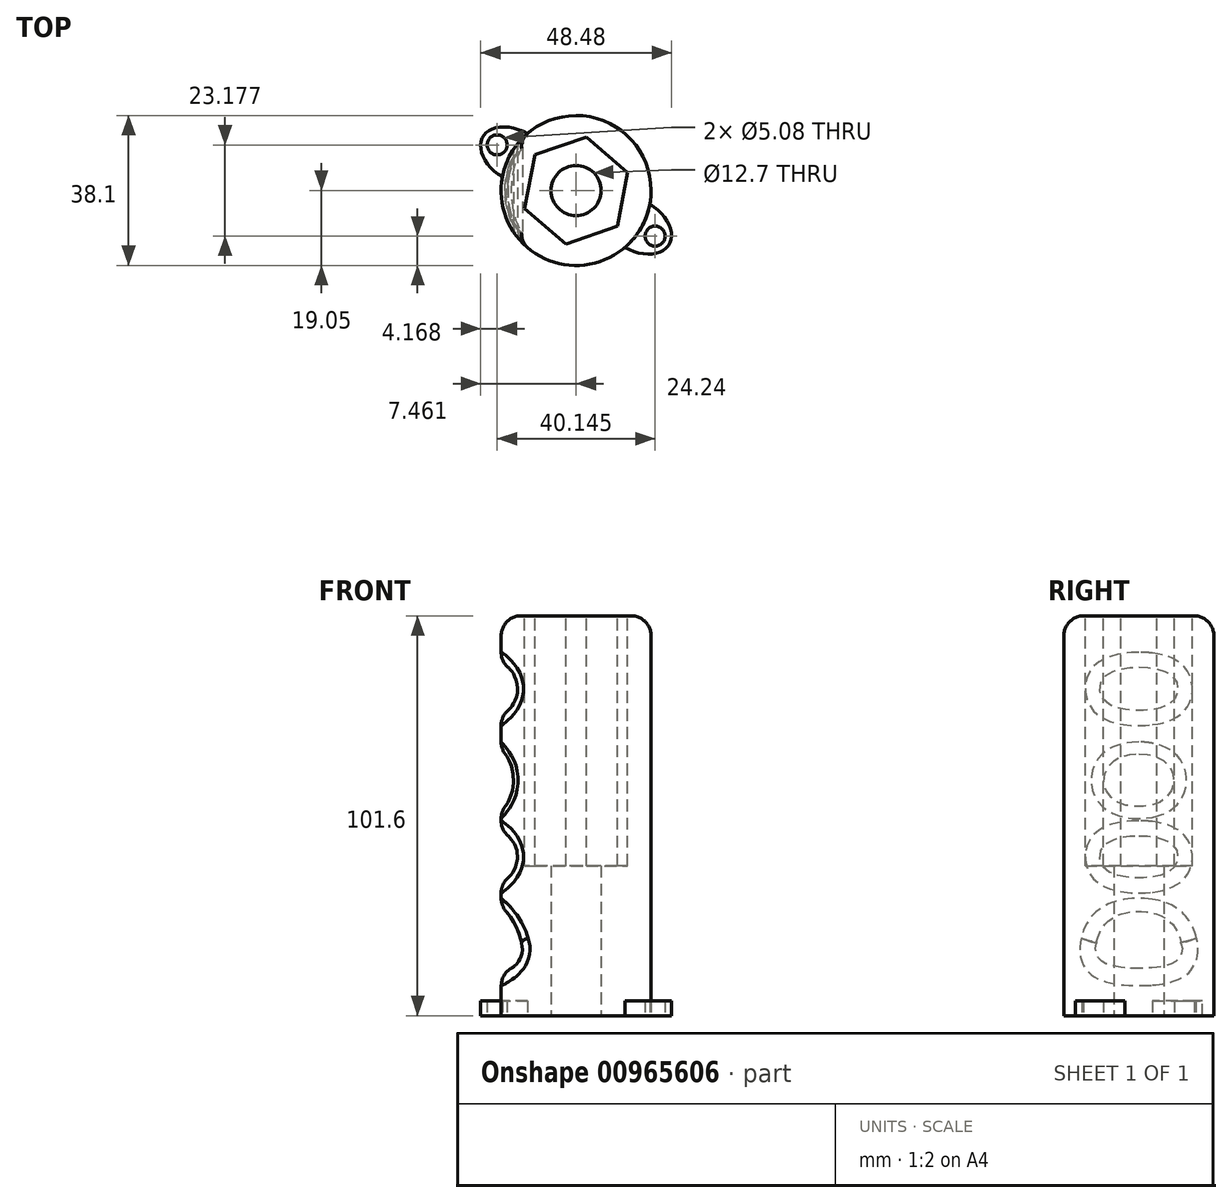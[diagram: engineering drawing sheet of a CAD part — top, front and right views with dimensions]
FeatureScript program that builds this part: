
annotation { "Feature Type Name" : "Feature", "Feature Type Description" : "" }
export const myFeature = defineFeature(function(context is Context, id is Id, definition is map)
    precondition{}
    {
        {
            var Q0;
            Q0=qCreatedBy(makeId("Top.planeOp"),FACE);
            var sketch = newSketch(context, id + "F0", { "sketchPlane" : qUnion([Q0])});
            skCircle(sketch, "E0", {"center": v(0, 0) * mm, "radius": 19.05 * mm});
            skSolve(sketch);
        }
        {
            var Q0;
            Q0=makeQuery(id+"F0.imprint","IMPRINT",FACE,{"disambiguationData":[TD([[makeQuery(id+"F0.imprint","IMPRINT",EDGE,{"derivedFrom":sQuery(id+"F0.wireOp",EDGE,"E0")}),1.0]])]});
            extrude(context, id + "F1", {"entities" : qUnion([Q0]), "depth" : 101.6 * mm, "offsetDistance" : 25.4 * mm});
        }
        {
            var Q0;
            Q0=qCreatedBy(makeId("Front.planeOp"),FACE);
            cPlane(context, id + "F2", {"entities" : qUnion([Q0]), "cplaneType" : CPlaneType.OFFSET, "offset" : 19.05 * mm, "width" : 152.4 * mm, "height" : 152.4 * mm});
        }
        {
            var Q0;
            Q0=qCreatedBy(id+"F2.planeOp",FACE);
            var sketch = newSketch(context, id + "F3", { "sketchPlane" : qUnion([Q0])});
            skLineSegment(sketch, "E1", {"start": v(0, 0) * mm, "end": v(-12.7, 0) * mm});
            skLineSegment(sketch, "E2", {"start": v(0, 0) * mm, "end": v(-16.51, 0) * mm});
            skLineSegment(sketch, "E3", {"start": v(-19.05, 0) * mm, "end": v(-19.05, 101.6) * mm});
            skLineSegment(sketch, "E4.0", {"start": v(-19.05, 101.6) * mm, "end": v(19.05, 101.6) * mm});
            skLineSegment(sketch, "E5", {"start": v(-16.51, 0) * mm, "end": v(-16.51, 101.6) * mm, "construction": true});
            skLineSegment(sketch, "E6", {"start": v(-12.7, 0) * mm, "end": v(-12.7, 101.6) * mm});
            skLineSegment(sketch, "E7", {"start": v(0, 0) * mm, "end": v(19.05, 0) * mm});
            skLineSegment(sketch, "E8", {"start": v(19.05, 0) * mm, "end": v(19.05, 11.29) * mm});
            skLineSegment(sketch, "E9", {"start": v(19.05, 11.29) * mm, "end": v(19.05, 22.58) * mm});
            skLineSegment(sketch, "E10", {"start": v(19.05, 22.58) * mm, "end": v(19.05, 33.87) * mm});
            skLineSegment(sketch, "E11", {"start": v(19.05, 45.16) * mm, "end": v(19.05, 56.44) * mm});
            skLineSegment(sketch, "E12", {"start": v(19.05, 56.44) * mm, "end": v(19.05, 67.73) * mm});
            skLineSegment(sketch, "E13", {"start": v(19.05, 67.73) * mm, "end": v(19.05, 79.02) * mm});
            skLineSegment(sketch, "E14", {"start": v(19.05, 79.02) * mm, "end": v(19.05, 90.31) * mm});
            skLineSegment(sketch, "E15", {"start": v(19.05, 33.87) * mm, "end": v(19.05, 45.16) * mm});
            skLineSegment(sketch, "E16", {"start": v(19.05, 90.31) * mm, "end": v(19.05, 101.6) * mm});
            skArc(sketch, "E17", {"start": v(-19.05, 11.29) * mm, "mid": v(-14.7, 13.66) * mm, "end": v(-13.9, 18.54) * mm});
            skArc(sketch, "E18", {"start": v(-19.05, 33.87) * mm, "mid": v(-14.87, 40.34) * mm, "end": v(-19.05, 46.82) * mm});
            skArc(sketch, "E19", {"start": v(-19.05, 51.93) * mm, "mid": v(-15.88, 59.82) * mm, "end": v(-19.05, 67.71) * mm});
            skArc(sketch, "E20", {"start": v(-19.05, 76.38) * mm, "mid": v(-14.87, 83.03) * mm, "end": v(-19.05, 89.68) * mm});
            skArc(sketch, "E21", {"start": v(-13.9, 18.54) * mm, "mid": v(-15.74, 23.57) * mm, "end": v(-19.05, 27.79) * mm});
            skPoint(sketch, "E22.orphan", {"position": v(-19.05, 22.58) * mm});
            skSolve(sketch);
        }
        {
            var Q0;
            {var subQ0=sQuery(id+"F3.wireOp",EDGE,"E17");Q0=makeQuery(id+"F3.imprint","IMPRINT",FACE,{"disambiguationData":[TD([[makeQuery(id+"F3.imprint","IMPRINT",EDGE,{"derivedFrom":subQ0}),1.0]])]});}
            var Q1;
            {var subQ0=sQuery(id+"F3.wireOp",EDGE,"E18");Q1=makeQuery(id+"F3.imprint","IMPRINT",FACE,{"disambiguationData":[TD([[makeQuery(id+"F3.imprint","IMPRINT",EDGE,{"derivedFrom":subQ0}),1.0]])]});}
            var Q2;
            {var subQ0=sQuery(id+"F3.wireOp",EDGE,"E19");Q2=makeQuery(id+"F3.imprint","IMPRINT",FACE,{"disambiguationData":[TD([[makeQuery(id+"F3.imprint","IMPRINT",EDGE,{"derivedFrom":subQ0}),1.0]])]});}
            var Q3;
            {var subQ0=sQuery(id+"F3.wireOp",EDGE,"E20");Q3=makeQuery(id+"F3.imprint","IMPRINT",FACE,{"disambiguationData":[TD([[makeQuery(id+"F3.imprint","IMPRINT",EDGE,{"derivedFrom":subQ0}),1.0]])]});}
            extrude(context, id + "F4", {"entities" : qUnion([Q0, Q1, Q2, Q3]), "operationType" : NewBodyOperationType.REMOVE, "oppositeDirection" : true, "depth" : 50.8 * mm, "offsetDistance" : 25.4 * mm});
        }
        {
            var Q0;
            Q0=makeQuery(id+"F4.boolean.opBoolean","INTERSECT",EDGE,{"derivedFrom":[makeQuery(id+"F1.opExtrude","SWEPT_FACE",FACE,{"disambiguationData":[OSD([sQuery(id+"F0.wireOp",EDGE,"E0")])]}),makeQuery(id+"F4.opExtrude","SWEPT_FACE",FACE,{"disambiguationData":[OSD([sQuery(id+"F3.wireOp",EDGE,"E18")])]})]});
            var Q1;
            Q1=makeQuery(id+"F4.boolean.opBoolean","INTERSECT",EDGE,{"derivedFrom":[makeQuery(id+"F1.opExtrude","SWEPT_FACE",FACE,{"disambiguationData":[OSD([sQuery(id+"F0.wireOp",EDGE,"E0")])]}),makeQuery(id+"F4.opExtrude","SWEPT_FACE",FACE,{"disambiguationData":[OSD([sQuery(id+"F3.wireOp",EDGE,"E19")])]})]});
            var Q2;
            Q2=makeQuery(id+"F4.boolean.opBoolean","INTERSECT",EDGE,{"derivedFrom":[makeQuery(id+"F1.opExtrude","SWEPT_FACE",FACE,{"disambiguationData":[OSD([sQuery(id+"F0.wireOp",EDGE,"E0")])]}),makeQuery(id+"F4.opExtrude","SWEPT_FACE",FACE,{"disambiguationData":[OSD([sQuery(id+"F3.wireOp",EDGE,"E20")])]})]});
            var Q3;
            Q3=makeQuery(id+"F4.boolean.opBoolean","COPY",EDGE,{"derivedFrom":makeQuery(id+"F4.opExtrude","SWEPT_EDGE",EDGE,{"disambiguationData":[OSD([sQuery(id+"F3.wireOp",EDGE,"E17"),sQuery(id+"F3.wireOp",EDGE,"E21")])]})});
            var Q4;
            Q4=makeQuery(id+"F4.boolean.opBoolean","INTERSECT",EDGE,{"derivedFrom":[makeQuery(id+"F1.opExtrude","SWEPT_FACE",FACE,{"disambiguationData":[OSD([sQuery(id+"F0.wireOp",EDGE,"E0")])]}),makeQuery(id+"F4.opExtrude","SWEPT_FACE",FACE,{"disambiguationData":[OSD([sQuery(id+"F3.wireOp",EDGE,"E17")])]})]});
            var Q5;
            Q5=makeQuery(id+"F4.boolean.opBoolean","INTERSECT",EDGE,{"derivedFrom":[makeQuery(id+"F1.opExtrude","SWEPT_FACE",FACE,{"disambiguationData":[OSD([sQuery(id+"F0.wireOp",EDGE,"E0")])]}),makeQuery(id+"F4.opExtrude","SWEPT_FACE",FACE,{"disambiguationData":[OSD([sQuery(id+"F3.wireOp",EDGE,"E21")])]})]});
            fillet(context, id + "F5", {"entities" : qUnion([Q0, Q1, Q2, Q3, Q4, Q5]), "radius" : 5.08 * mm, "tangentPropagation" : true, "defaultsChanged" : false, "vertexSettings" : [], "allowEdgeOverflow" : false});
        }
        {
            var Q0;
            Q0=makeQuery(id+"F1.opExtrude","CAP_FACE",FACE,{"disambiguationData":[OSD([sQuery(id+"F0.wireOp",EDGE,"E0")])],"isStart":true});
            var sketch = newSketch(context, id + "F6", { "sketchPlane" : qUnion([Q0])});
            skLineSegment(sketch, "E23", {"start": v(0, 0) * mm, "end": v(0, 17.78) * mm});
            skLineSegment(sketch, "E24", {"start": v(0, 0) * mm, "end": v(-5.87, 0) * mm});
            skCircle(sketch, "E25.0.0", {"center": v(0, 0) * mm, "radius": 19.05 * mm});
            skLineSegment(sketch, "E26", {"start": v(0, 0) * mm, "end": v(17.78, 0) * mm});
            skEllipse(sketch, "E27.MirrorC", {"center": v(-15.4, -8.9) * mm, "majorRadius": 9.53 * mm, "minorRadius": 6.35 * mm, "majorAxis": v(-0.87, -0.5)});
            skLineSegment(sketch, "E28", {"start": v(0, 0) * mm, "end": v(21.59, 0) * mm, "construction": true});
            skLineSegment(sketch, "E29", {"start": v(-15.4, -8.9) * mm, "end": v(0, 0) * mm});
            skLineSegment(sketch, "E30", {"start": v(0, 0) * mm, "end": v(5.2, -9) * mm});
            skEllipse(sketch, "E31.MirrorC", {"center": v(15.4, 8.9) * mm, "majorRadius": 9.53 * mm, "minorRadius": 6.35 * mm, "majorAxis": v(0.87, 0.5)});
            skLineSegment(sketch, "E32", {"start": v(-15.4, -8.9) * mm, "end": v(-7.15, -4.13) * mm});
            skLineSegment(sketch, "E33", {"start": v(-23.65, -13.65) * mm, "end": v(-16.5, -9.53) * mm});
            skPoint(sketch, "E34", {"position": v(-20.07, -11.59) * mm});
            skPoint(sketch, "E35.MirrorP", {"position": v(20.07, 11.59) * mm});
            skSolve(sketch);
        }
        {
            var Q0;
            {var subQ0=sQuery(id+"FZY5milzs4ELDXf_1.wireOp",EDGE,"5038e947-432d-46be-ba0d-5f1da9be2be5.0.0");Q0=makeQuery(id+"FJVRa8w2PpgUHNq_1.boolean.opBoolean","MERGE",FACE,{"derivedFrom":[makeQuery(id+"F1.opExtrude","CAP_FACE",FACE,{"disambiguationData":[OSD([sQuery(id+"F0.wireOp",EDGE,"E0")])],"isStart":false}),makeQuery(id+"FJVRa8w2PpgUHNq_1.opExtrude","CAP_FACE",FACE,{"disambiguationData":[OSD([sQuery(id+"FZY5milzs4ELDXf_1.wireOp",EDGE,"e975b173-eecc-4d75-a19c-4a433cebcd96.0.0"),subQ0])],"isStart":true}),makeQuery(id+"FJVRa8w2PpgUHNq_1.opExtrude","CAP_FACE",FACE,{"disambiguationData":[OSD([sQuery(id+"FZY5milzs4ELDXf_1.wireOp",EDGE,"1aa8e91c-0e7e-4a1b-bd8e-dbe82b9d2f2e.0.0"),subQ0])],"isStart":true})]});}
            fillet(context, id + "F7", {"entities" : qUnion([Q0]), "radius" : 5.08 * mm, "tangentPropagation" : true, "allowEdgeOverflow" : false});
        }
        {
            var Q0;
            {var subQ0=sQuery(id+"F6.wireOp",EDGE,"E25.0.0");var subQ1=sQuery(id+"F6.wireOp",EDGE,"E27.MirrorC");var subQ2=makeQuery(id+"F6.imprint","INTERSECT",VERTEX,{"disambiguationData":[OD(0.0)],"derivedFrom":[subQ1,subQ0]});Q0=makeQuery(id+"F6.imprint","IMPRINT",FACE,{"disambiguationData":[TD([[makeQuery(id+"F6.imprint","IMPRINT",EDGE,{"disambiguationData":[TD([[subQ2,1.0]])],"derivedFrom":subQ1}),1.0]])]});}
            var Q1;
            {var subQ0=sQuery(id+"F6.wireOp",EDGE,"E25.0.0");var subQ1=sQuery(id+"F6.wireOp",EDGE,"foFyNaQt-y216-XrTq-2MQ0-xOWPkpz0StqU");var subQ2=makeQuery(id+"F6.imprint","INTERSECT",VERTEX,{"disambiguationData":[OD(0.0)],"derivedFrom":[subQ1,subQ0]});Q1=makeQuery(id+"F6.imprint","IMPRINT",FACE,{"disambiguationData":[TD([[makeQuery(id+"F6.imprint","IMPRINT",EDGE,{"disambiguationData":[TD([[subQ2,1.0]])],"derivedFrom":subQ1}),1.0]])]});}
            var Q2;
            {var subQ0=sQuery(id+"F6.wireOp",EDGE,"E31.MirrorC");var subQ1=sQuery(id+"F6.wireOp",EDGE,"E25.0.0");var subQ2=makeQuery(id+"F6.imprint","INTERSECT",VERTEX,{"disambiguationData":[OD(0.0)],"derivedFrom":[subQ1,subQ0]});Q2=makeQuery(id+"F6.imprint","IMPRINT",FACE,{"disambiguationData":[TD([[makeQuery(id+"F6.imprint","IMPRINT",EDGE,{"disambiguationData":[TD([[subQ2,-1.0]])],"derivedFrom":subQ1}),1.0]])]});}
            var Q3;
            {var subQ0=sQuery(id+"F6.wireOp",EDGE,"E33");Q3=makeQuery(id+"F6.imprint","IMPRINT",FACE,{"disambiguationData":[TD([[makeQuery(id+"F6.imprint","IMPRINT",EDGE,{"derivedFrom":subQ0}),1.0]])]});}
            extrude(context, id + "F8", {"entities" : qUnion([Q0, Q1, Q2, Q3]), "operationType" : NewBodyOperationType.ADD, "oppositeDirection" : true, "depth" : 3.8 * mm, "offsetDistance" : 25.4 * mm});
        }
        {
            var Q0;
            Q0=sQuery(id+"F6.wireOp",VERTEX,"E34");
            var Q1;
            Q1=sQuery(id+"F6.wireOp",VERTEX,"E35.MirrorP");
            var Q2;
            Q2=makeQuery(id+"F1.opExtrude","SWEPT_BODY",BODY,{"disambiguationData":[OSD([sQuery(id+"F0.wireOp",EDGE,"E0")])]});
            hole(context, id + "F9", {"style" : HoleStyle.SIMPLE, "endStyle" : HoleEndStyle.THROUGH, "holeDiameter" : 5.08 * mm, "majorDiameter" : 6.35 * mm, "isTappedThrough" : true, "tappedDepth" : 12.7 * mm, "tapClearance" : 3, "locations" : qUnion([Q0, Q1]), "scope" : qUnion([Q2])});
        }
        {
            var Q0;
            Q0=makeQuery(id+"F1.opExtrude","CAP_FACE",FACE,{"disambiguationData":[OSD([sQuery(id+"F0.wireOp",EDGE,"E0")])],"isStart":false});
            var sketch = newSketch(context, id + "F10", { "sketchPlane" : qUnion([Q0])});
            skCircle(sketch, "E36.cCircle", {"center": v(0, 0) * mm, "radius": 12 * mm, "construction": true});
            skLineSegment(sketch, "E36.0", {"start": v(2.6, 13.6) * mm, "end": v(13.09, 4.55) * mm});
            skLineSegment(sketch, "E36.1", {"start": v(13.09, 4.55) * mm, "end": v(10.48, -9.06) * mm});
            skLineSegment(sketch, "E36.2", {"start": v(10.48, -9.06) * mm, "end": v(-2.6, -13.6) * mm});
            skLineSegment(sketch, "E36.3", {"start": v(-2.6, -13.6) * mm, "end": v(-13.09, -4.55) * mm});
            skLineSegment(sketch, "E36.4", {"start": v(-13.09, -4.55) * mm, "end": v(-10.48, 9.06) * mm});
            skLineSegment(sketch, "E36.5", {"start": v(-10.48, 9.06) * mm, "end": v(2.6, 13.6) * mm});
            skPoint(sketch, "E36.0.midPoint", {"position": v(7.85, 9.08) * mm});
            skSolve(sketch);
        }
        {
            var Q0;
            Q0=makeQuery(id+"F10.imprint","IMPRINT",FACE,{"disambiguationData":[TD([[makeQuery(id+"F10.imprint","IMPRINT",EDGE,{"derivedFrom":sQuery(id+"F10.wireOp",EDGE,"E36.0")}),-1.0]])]});
            extrude(context, id + "F11", {"entities" : qUnion([Q0]), "operationType" : NewBodyOperationType.REMOVE, "oppositeDirection" : true, "depth" : 63.5 * mm, "offsetDistance" : 25.4 * mm});
        }
        {
            var Q0;
            {var subQ0=sQuery(id+"F6.wireOp",EDGE,"E25.0.0");Q0=makeQuery(id+"F8.boolean.opBoolean","MERGE",FACE,{"derivedFrom":[makeQuery(id+"F1.opExtrude","CAP_FACE",FACE,{"disambiguationData":[OSD([sQuery(id+"F0.wireOp",EDGE,"E0")])],"isStart":true}),makeQuery(id+"F8.opExtrude","CAP_FACE",FACE,{"disambiguationData":[OSD([sQuery(id+"F6.wireOp",EDGE,"foFyNaQt-y216-XrTq-2MQ0-xOWPkpz0StqU"),subQ0])],"isStart":true}),makeQuery(id+"F8.opExtrude","CAP_FACE",FACE,{"disambiguationData":[OSD([sQuery(id+"F6.wireOp",EDGE,"E27.MirrorC"),subQ0])],"isStart":true})]});}
            var sketch = newSketch(context, id + "F12", { "sketchPlane" : qUnion([Q0])});
            skCircle(sketch, "E37", {"center": v(0, 0) * mm, "radius": 6.35 * mm});
            skSolve(sketch);
        }
        {
            var Q0;
            Q0=makeQuery(id+"F12.imprint","IMPRINT",FACE,{"disambiguationData":[TD([[makeQuery(id+"F12.imprint","IMPRINT",EDGE,{"derivedFrom":sQuery(id+"F12.wireOp",EDGE,"E37")}),1.0]])]});
            extrude(context, id + "F13", {"entities" : qUnion([Q0]), "operationType" : NewBodyOperationType.REMOVE, "oppositeDirection" : true, "depth" : 127 * mm, "offsetDistance" : 25.4 * mm});
        }
    });
